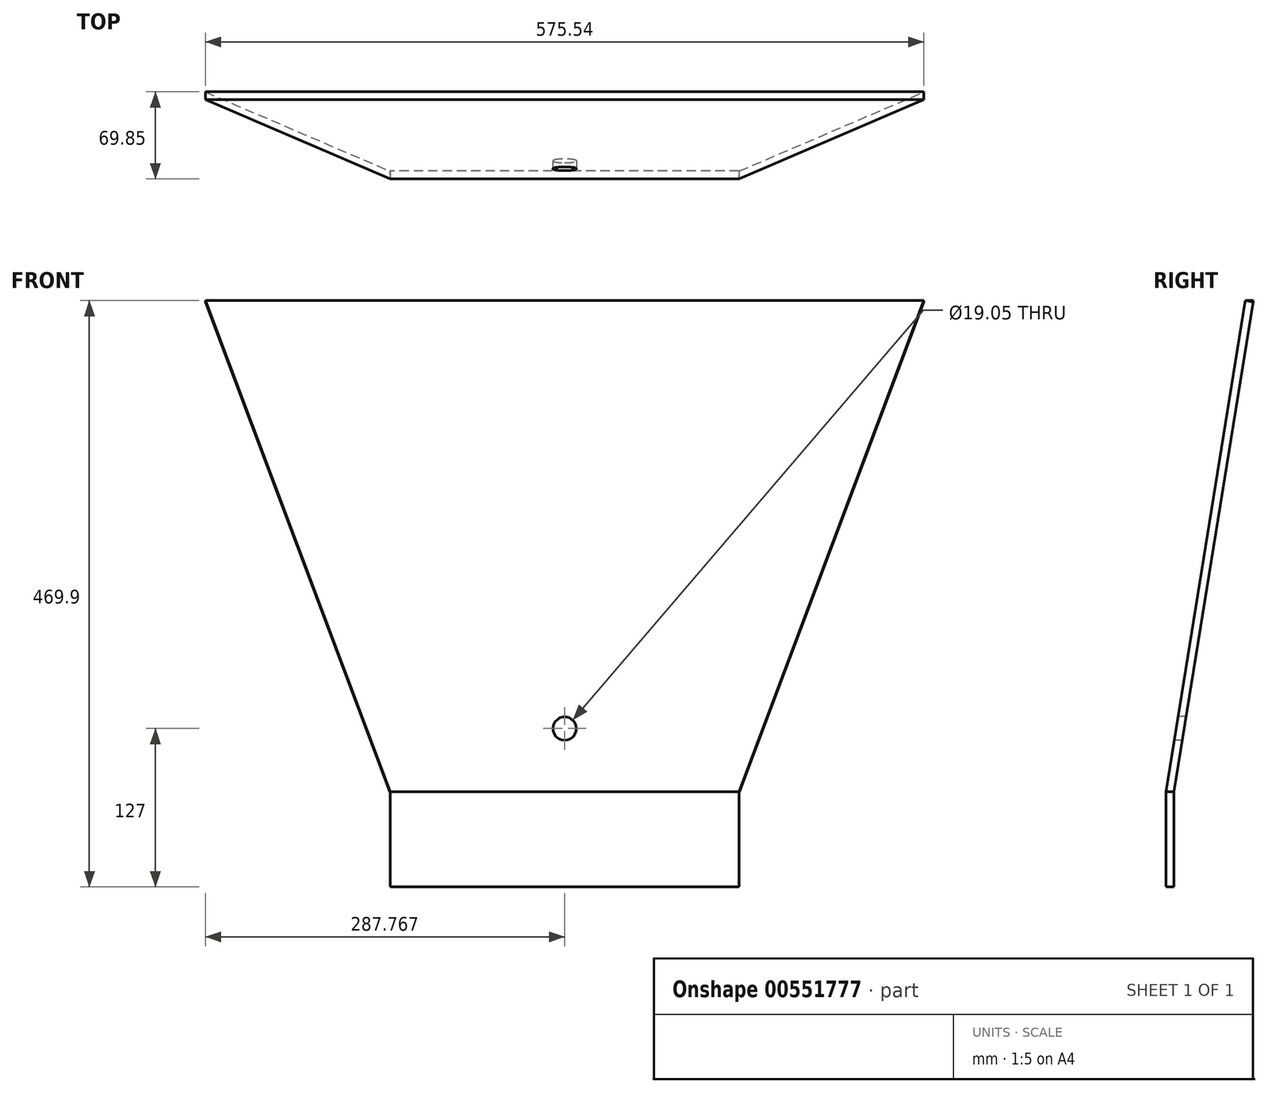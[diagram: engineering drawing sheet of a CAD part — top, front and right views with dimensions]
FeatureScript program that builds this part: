
annotation { "Feature Type Name" : "Feature", "Feature Type Description" : "" }
export const myFeature = defineFeature(function(context is Context, id is Id, definition is map)
    precondition{}
    {
        {
            var Q0;
            Q0=qCreatedBy(makeId("Right.planeOp"),FACE);
            var sketch = newSketch(context, id + "F0", { "sketchPlane" : qUnion([Q0])});
            skLineSegment(sketch, "E0", {"start": v(0, 0) * mm, "end": v(0, 76.2) * mm});
            skLineSegment(sketch, "E1", {"start": v(0, 0) * mm, "end": v(6.35, 0) * mm});
            skLineSegment(sketch, "E2", {"start": v(6.35, 0) * mm, "end": v(6.35, 76.2) * mm});
            skLineSegment(sketch, "E3", {"start": v(6.35, 76.2) * mm, "end": v(69.85, 469.9) * mm});
            skLineSegment(sketch, "E4", {"start": v(0, 76.2) * mm, "end": v(63.5, 469.9) * mm});
            skLineSegment(sketch, "E5", {"start": v(63.5, 469.9) * mm, "end": v(69.85, 469.9) * mm});
            skSolve(sketch);
        }
        {
            var Q0;
            Q0=makeQuery(id+"F0.imprint","IMPRINT",FACE,{"disambiguationData":[TD([[makeQuery(id+"F0.imprint","IMPRINT",EDGE,{"derivedFrom":sQuery(id+"F0.wireOp",EDGE,"E0")}),-1.0]])]});
            extrude(context, id + "F1", {"entities" : qUnion([Q0]), "depth" : 609.6 * mm, "offsetDistance" : 25.4 * mm});
        }
        {
            var Q0;
            Q0=makeQuery(id+"F1.opExtrude","SWEPT_FACE",FACE,{"disambiguationData":[OSD([sQuery(id+"F0.wireOp",EDGE,"E0")])]});
            var sketch = newSketch(context, id + "F2", { "sketchPlane" : qUnion([Q0])});
            skLineSegment(sketch, "E6", {"start": v(0, 482.6) * mm, "end": v(150.9, 76.2) * mm});
            skLineSegment(sketch, "E7", {"start": v(150.9, 76.2) * mm, "end": v(150.9, 0) * mm});
            skLineSegment(sketch, "E8", {"start": v(0, 482.6) * mm, "end": v(581.2, 482.6) * mm});
            skLineSegment(sketch, "E9", {"start": v(581.2, 482.6) * mm, "end": v(430.3, 76.2) * mm});
            skLineSegment(sketch, "E10", {"start": v(430.3, 76.2) * mm, "end": v(430.3, 0) * mm});
            skLineSegment(sketch, "E11", {"start": v(430.3, 0) * mm, "end": v(150.9, 0) * mm});
            skLineSegment(sketch, "E12", {"start": v(290.6, 482.6) * mm, "end": v(290.6, 0) * mm});
            skLineSegment(sketch, "E13", {"start": v(290.6, 0) * mm, "end": v(290.6, 152.4) * mm});
            skLineSegment(sketch, "E14", {"start": v(290.6, 0) * mm, "end": v(290.6, 190.5) * mm});
            skLineSegment(sketch, "E15", {"start": v(290.6, 152.4) * mm, "end": v(309.65, 152.4) * mm});
            skLineSegment(sketch, "E16", {"start": v(290.6, 152.4) * mm, "end": v(271.55, 152.4) * mm});
            skLineSegment(sketch, "E17", {"start": v(290.6, 482.6) * mm, "end": v(309.65, 482.6) * mm});
            skLineSegment(sketch, "E18", {"start": v(290.6, 482.6) * mm, "end": v(271.55, 482.6) * mm});
            skLineSegment(sketch, "E19", {"start": v(309.65, 482.6) * mm, "end": v(347.75, 190.5) * mm});
            skLineSegment(sketch, "E20", {"start": v(271.55, 482.6) * mm, "end": v(233.45, 190.5) * mm});
            skLineSegment(sketch, "E21", {"start": v(233.45, 190.5) * mm, "end": v(271.55, 152.4) * mm});
            skLineSegment(sketch, "E22", {"start": v(347.75, 190.5) * mm, "end": v(309.65, 152.4) * mm});
            skLineSegment(sketch, "E23", {"start": v(290.6, 0) * mm, "end": v(290.6, 127) * mm});
            skCircle(sketch, "E24", {"center": v(290.6, 127) * mm, "radius": 9.53 * mm});
            skSolve(sketch);
        }
        {
            var Q0;
            {var subQ1=sQuery(id+"F2.wireOp",EDGE,"E12");Q0=makeQuery(id+"F2.imprint","IMPRINT",FACE,{"disambiguationData":[TD([[makeQuery(id+"F2.imprint","IMPRINT",EDGE,{"derivedFrom":subQ1}),-1.0]])]});}
            var Q1;
            {var subQ2=sQuery(id+"F2.wireOp",EDGE,"E12");Q1=makeQuery(id+"F2.imprint","IMPRINT",FACE,{"disambiguationData":[TD([[makeQuery(id+"F2.imprint","IMPRINT",EDGE,{"derivedFrom":subQ2}),1.0]])]});}
            var Q2;
            {var subQ0=sQuery(id+"F2.wireOp",EDGE,"E23");var subQ1=sQuery(id+"F2.wireOp",EDGE,"E14");var subQ2=makeQuery(id+"F2.imprint","INTERSECT",VERTEX,{"derivedFrom":[subQ1,subQ0]});Q2=makeQuery(id+"F2.imprint","IMPRINT",FACE,{"disambiguationData":[TD([[makeQuery(id+"F2.imprint","IMPRINT",EDGE,{"disambiguationData":[TD([[subQ2,-1.0]])],"derivedFrom":subQ1}),-1.0]])]});}
            var Q3;
            {var subQ0=sQuery(id+"F2.wireOp",EDGE,"E23");var subQ1=sQuery(id+"F2.wireOp",EDGE,"E14");var subQ2=makeQuery(id+"F2.imprint","INTERSECT",VERTEX,{"derivedFrom":[subQ1,subQ0]});Q3=makeQuery(id+"F2.imprint","IMPRINT",FACE,{"disambiguationData":[TD([[makeQuery(id+"F2.imprint","IMPRINT",EDGE,{"disambiguationData":[TD([[subQ2,-1.0]])],"derivedFrom":subQ1}),1.0]])]});}
            var Q4;
            {var subQ0=sQuery(id+"F2.wireOp",EDGE,"E10");Q4=makeQuery(id+"F2.imprint","IMPRINT",FACE,{"disambiguationData":[TD([[makeQuery(id+"F2.imprint","IMPRINT",EDGE,{"derivedFrom":subQ0}),1.0]])]});}
            var Q5;
            {var subQ0=sQuery(id+"F2.wireOp",EDGE,"E7");Q5=makeQuery(id+"F2.imprint","IMPRINT",FACE,{"disambiguationData":[TD([[makeQuery(id+"F2.imprint","IMPRINT",EDGE,{"derivedFrom":subQ0}),-1.0]])]});}
            extrude(context, id + "F3", {"entities" : qUnion([Q0, Q1, Q2, Q3, Q4, Q5]), "operationType" : NewBodyOperationType.REMOVE, "oppositeDirection" : true, "depth" : 228.6 * mm, "offsetDistance" : 25.4 * mm});
        }
        {
            var Q0;
            Q0=makeQuery(id+"F1.opExtrude","SWEPT_FACE",FACE,{"disambiguationData":[OSD([sQuery(id+"F0.wireOp",EDGE,"E4")])]});
            var sketch = newSketch(context, id + "F4", { "sketchPlane" : qUnion([Q0])});
            skLineSegment(sketch, "E25", {"start": v(-9.43, 507.03) * mm, "end": v(150.9, 75.23) * mm});
            skLineSegment(sketch, "E26", {"start": v(590.62, 507.03) * mm, "end": v(430.3, 75.23) * mm});
            skSolve(sketch);
        }
        {
            var Q0;
            {var subQ1=sQuery(id+"F0.wireOp",EDGE,"E4");var subQ8=makeQuery(id+"F1.opExtrude","CAP_EDGE",EDGE,{"disambiguationData":[OSD([subQ1])],"isStart":true});Q0=makeQuery(id+"F4.imprint","IMPRINT",FACE,{"disambiguationData":[TD([[makeQuery(id+"F4.imprint","IMPRINT",EDGE,{"derivedFrom":subQ8}),-1.0]])]});}
            extrude(context, id + "F5", {"entities" : qUnion([Q0]), "operationType" : NewBodyOperationType.REMOVE, "oppositeDirection" : true, "depth" : 121.92 * mm, "offsetDistance" : 25.4 * mm});
        }
        {
            var Q0;
            Q0=makeQuery(id+"F1.opExtrude","SWEPT_FACE",FACE,{"disambiguationData":[OSD([sQuery(id+"F0.wireOp",EDGE,"E4")])]});
            var sketch = newSketch(context, id + "F6", { "sketchPlane" : qUnion([Q0])});
            skLineSegment(sketch, "E27", {"start": v(430.3, 75.23) * mm, "end": v(590.62, 507.03) * mm});
            skSolve(sketch);
        }
        {
            var Q0;
            {var subQ1=sQuery(id+"F0.wireOp",EDGE,"E4");var subQ8=makeQuery(id+"F1.opExtrude","CAP_EDGE",EDGE,{"disambiguationData":[OSD([subQ1])],"isStart":false});Q0=makeQuery(id+"F6.imprint","IMPRINT",FACE,{"disambiguationData":[TD([[makeQuery(id+"F6.imprint","IMPRINT",EDGE,{"derivedFrom":subQ8}),1.0]])]});}
            extrude(context, id + "F7", {"entities" : qUnion([Q0]), "operationType" : NewBodyOperationType.REMOVE, "oppositeDirection" : true, "depth" : 162.56 * mm, "offsetDistance" : 25.4 * mm});
        }
        {
            var Q0;
            {var subQ0=sQuery(id+"F0.wireOp",EDGE,"E5");Q0=makeQuery(id+"F3.boolean.opBoolean","SPLIT",FACE,{"disambiguationData":[TD([makeQuery(id+"F3.opExtrude","SWEPT_FACE",FACE,{"disambiguationData":[OSD([sQuery(id+"F2.wireOp",EDGE,"E19")])]})])],"derivedFrom":makeQuery(id+"F1.opExtrude","SWEPT_FACE",FACE,{"disambiguationData":[OSD([subQ0])]})});}
            var sketch = newSketch(context, id + "F8", { "sketchPlane" : qUnion([Q0])});
            skLineSegment(sketch, "E28", {"start": v(578.37, 63.5) * mm, "end": v(578.37, 69.85) * mm});
            skLineSegment(sketch, "E29", {"start": v(578.37, 69.85) * mm, "end": v(609.6, 69.85) * mm});
            skLineSegment(sketch, "E30", {"start": v(609.6, 69.85) * mm, "end": v(609.6, 63.5) * mm});
            skLineSegment(sketch, "E31", {"start": v(609.6, 63.5) * mm, "end": v(578.37, 63.5) * mm});
            skSolve(sketch);
        }
        {
            var Q0;
            Q0=makeQuery(id+"F8.imprint","IMPRINT",FACE,{"disambiguationData":[TD([[makeQuery(id+"F8.imprint","IMPRINT",EDGE,{"derivedFrom":sQuery(id+"F8.wireOp",EDGE,"E28")}),-1.0]])]});
            extrude(context, id + "F9", {"entities" : qUnion([Q0]), "operationType" : NewBodyOperationType.REMOVE, "oppositeDirection" : true, "depth" : 25.4 * mm, "offsetDistance" : 25.4 * mm});
        }
        {
            var Q0;
            {var subQ0=sQuery(id+"F0.wireOp",EDGE,"E5");Q0=makeQuery(id+"F3.boolean.opBoolean","SPLIT",FACE,{"disambiguationData":[TD([makeQuery(id+"F3.opExtrude","SWEPT_FACE",FACE,{"disambiguationData":[OSD([sQuery(id+"F2.wireOp",EDGE,"E20")])]})])],"derivedFrom":makeQuery(id+"F1.opExtrude","SWEPT_FACE",FACE,{"disambiguationData":[OSD([subQ0])]})});}
            var sketch = newSketch(context, id + "F10", { "sketchPlane" : qUnion([Q0])});
            skLineSegment(sketch, "E32", {"start": v(2.83, 63.5) * mm, "end": v(2.83, 69.85) * mm});
            skLineSegment(sketch, "E33", {"start": v(2.83, 69.85) * mm, "end": v(0, 69.85) * mm});
            skLineSegment(sketch, "E34", {"start": v(0, 69.85) * mm, "end": v(0, 63.5) * mm});
            skLineSegment(sketch, "E35", {"start": v(0, 63.5) * mm, "end": v(2.83, 63.5) * mm});
            skSolve(sketch);
        }
        {
            var Q0;
            Q0 = qSketchRegion(id + "F10", true);
            extrude(context, id + "F11", {"entities" : qUnion([Q0]), "operationType" : NewBodyOperationType.REMOVE, "oppositeDirection" : true, "depth" : 25.4 * mm, "offsetDistance" : 25.4 * mm});
        }
    });
